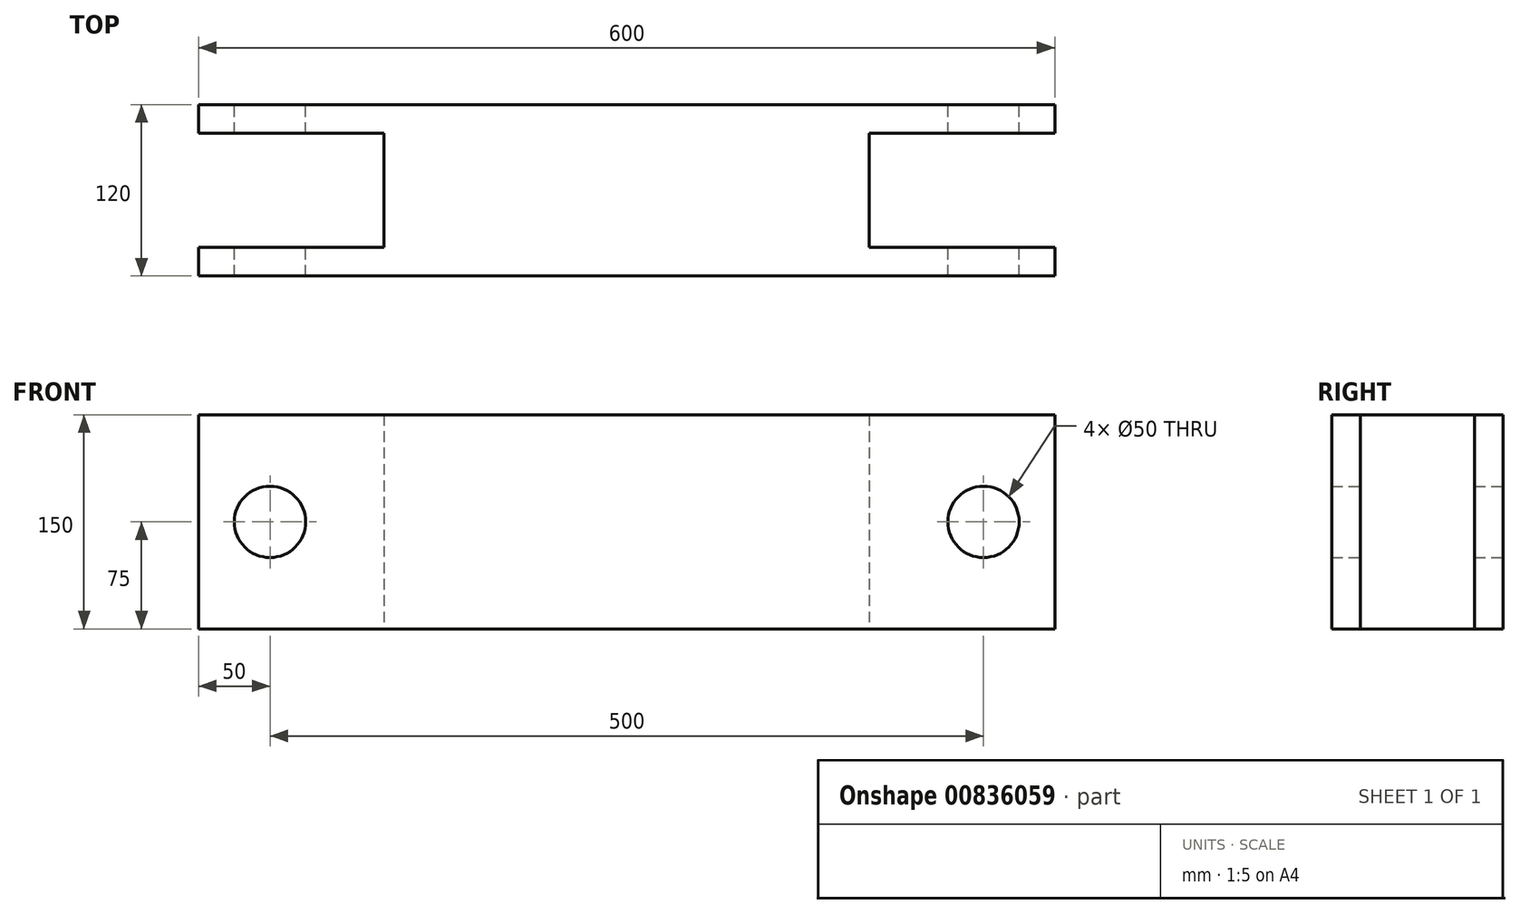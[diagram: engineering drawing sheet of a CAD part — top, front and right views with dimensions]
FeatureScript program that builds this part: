
annotation { "Feature Type Name" : "Feature", "Feature Type Description" : "" }
export const myFeature = defineFeature(function(context is Context, id is Id, definition is map)
    precondition{}
    {
        {
            var Q0;
            Q0=qCreatedBy(makeId("Front.planeOp"),FACE);
            var sketch = newSketch(context, id + "F0", { "sketchPlane" : qUnion([Q0])});
            skLineSegment(sketch, "E0.bottom", {"start": v(-300, 75) * mm, "end": v(0, 75) * mm});
            skLineSegment(sketch, "E0.top", {"start": v(-300, -75) * mm, "end": v(0, -75) * mm});
            skLineSegment(sketch, "E0.left", {"start": v(-300, 75) * mm, "end": v(-300, -75) * mm});
            skPoint(sketch, "E0.middle", {"position": v(0, 0) * mm});
            skLineSegment(sketch, "E1", {"start": v(0, 75) * mm, "end": v(0, -75) * mm});
            skCircle(sketch, "E2", {"center": v(-250, 0) * mm, "radius": 25 * mm});
            skPoint(sketch, "E3.end.orphan", {"position": v(-300, 0) * mm});
            skSolve(sketch);
        }
        {
            var Q0;
            Q0=makeQuery(id+"F0.imprint","IMPRINT",FACE,{"disambiguationData":[TD([[makeQuery(id+"F0.imprint","IMPRINT",EDGE,{"derivedFrom":sQuery(id+"F0.wireOp",EDGE,"E0.bottom")}),-1.0]])]});
            extrude(context, id + "F1", {"entities" : qUnion([Q0]), "endBound" : BoundingType.SYMMETRIC, "depth" : 120 * mm, "offsetDistance" : 25 * mm});
        }
        {
            var Q0;
            Q0=qCreatedBy(makeId("Front.planeOp"),FACE);
            var sketch = newSketch(context, id + "F2", { "sketchPlane" : qUnion([Q0])});
            skLineSegment(sketch, "E4.bottom", {"start": v(-300, 75) * mm, "end": v(-170, 75) * mm});
            skLineSegment(sketch, "E4.top", {"start": v(-300, -75) * mm, "end": v(-170, -75) * mm});
            skLineSegment(sketch, "E4.left", {"start": v(-300, 75) * mm, "end": v(-300, -75) * mm});
            skLineSegment(sketch, "E4.right", {"start": v(-170, 75) * mm, "end": v(-170, -75) * mm});
            skCircle(sketch, "E5", {"center": v(-250, 0) * mm, "radius": 25 * mm});
            skSolve(sketch);
        }
        {
            var Q0;
            Q0 = qSketchRegion(id + "F2", true);
            extrude(context, id + "F3", {"entities" : qUnion([Q0]), "operationType" : NewBodyOperationType.REMOVE, "endBound" : BoundingType.SYMMETRIC, "oppositeDirection" : true, "depth" : 80 * mm, "offsetDistance" : 25 * mm});
        }
        {
            var Q0;
            Q0=makeQuery(id+"F1.opExtrude","SWEPT_BODY",BODY,{"disambiguationData":[OSD([sQuery(id+"F0.wireOp",EDGE,"E0.bottom"),sQuery(id+"F0.wireOp",EDGE,"E0.top"),sQuery(id+"F0.wireOp",EDGE,"E0.left"),sQuery(id+"F0.wireOp",EDGE,"E1"),sQuery(id+"F0.wireOp",EDGE,"E2")])]});
            var Q1;
            Q1=makeQuery(id+"F1.opExtrude","SWEPT_FACE",FACE,{"disambiguationData":[OSD([sQuery(id+"F0.wireOp",EDGE,"E1")])]});
            mirror(context, id + "F4", {"operationType" : NewBodyOperationType.ADD, "entities" : qUnion([Q0]), "mirrorPlane" : qUnion([Q1])});
        }
    });
